# Revit family: Ventüer_VentilationLouvres_VL-50PL
name_source: partatom
category: Generic Models
units: mm (PartAtom-declared; Revit-internal decimal feet)

## family parameters
Always vertical = No
Can host rebar = No
Cut with Voids When Loaded = No
Part Type = Normal
Room Calculation Point = No
Round Connector Dimension = Use Diameter
Shared = No
Work Plane-Based = Yes

## types (2) — shared parameters
Aerodynamic Performance = VL-50PL1 – Coefficient of Entry: 0.281. VL-50PL2 – Coefficient of Entry: 0.285. VL-50PL3 – Coefficient of Entry: 0.253. VL-50PL4 – Coefficient of Entry: 0.287. VL-50PL5 – Coefficient of Entry: 0.258. VL-50PL6 – Coefficient of Entry: 0.264
Ancillaries = Bird Mesh, Insect Mesh, Solid Blanking, Perimeter Mounting Angle
Blade And Frame Gap = 16 mm
Blade Centres = 50 mm  [stored 0.164042 ft]
Blade Material = Ventüer Aluminium
Default Elevation = 1219 mm
Description = The Invisible Louvre
Exact Neck Height = 594 mm  [stored 1.94882 ft]
Exact Neck Height Check = 594 mm  [stored 1.94882 ft]
Exact Neck Width = 594 mm  [stored 1.94882 ft]
Exact Neck Width Check = 594 mm  [stored 1.94882 ft]
Face Panel = Ventüer Transparent
Frame Material = Ventüer Aluminium
Frame Set Count = 1
Frame Set Count Check = 2
Frame Set Transition Count = 1
Frame Set Transition Count Check = 2
Keynote = VL-50PL_FF
Manufacturer = Ventüer
Max Flow = 5000.0 L/s
Min Flow = 100.0 L/s
Model = VL-50PL
Multiple Frame Set = No
Multiple Transition = No
Noise Level NC Max = 0.00 NC
Noise Level NC Min = 0.00 NC
Nominal Height = 600 mm
Nominal Width = 600 mm
Nominated Air Flow = 100.0 L/s
Nominated Pessure Drop = 21.0 Pa
Rain Defence Performance = Class B – up to 1.0m/s suction velocity. Class C – up to 2.5m/s suction velocity. Class D – up to 3.5m/s suction velocity
Single Frame Set = Yes
Single Transition = No
Specified Air Flow = 0.0 L/s
Specified Pressure Drop = 21.0 Pa
Static Pressure Max = 60.0 Pa
Static Pressure Min = 10.0 Pa
URL = https://www.ventuer.co
Ventüer Product Range = Ventilation Louvres

## per-type parameters (varying)
| type | Base Width | Blade Count | Blade Cut Offset | Blade Length | Connector Height | Connector Width | Depth | Flanged | Frame Set Height | Frame Set Width | Glazed | Overall Opening Height | Overall Opening Width | Perforated Pattern Height | Perforated Pattern Width | Profile Width | Rear Frame Set Offset | Rear Mullion Offset | Single Frame Set Width | Top Blade Height |
| VL-50PL_FF | 52 mm | 9 | 450 mm  [stored 1.47638 ft] | 484 mm  [stored 1.58793 ft] | 490 mm  [stored 1.60761 ft] | 490 mm  [stored 1.60761 ft] | 101 mm  [stored 0.331365 ft] | Yes | 490 mm  [stored 1.60761 ft] | 490 mm  [stored 1.60761 ft] | No | 490 mm  [stored 1.60761 ft] | 490 mm  [stored 1.60761 ft] | 493 mm  [stored 1.61745 ft] | 493 mm  [stored 1.61745 ft] | 52 mm | 3 mm  [stored 0.00984252 ft] | 2 mm  [stored 0.00656168 ft] | 245 mm | 24 mm |
| VL-50PL_GF | 26 mm | 10 | 500 mm  [stored 1.64042 ft] | 536 mm | 542 mm  [stored 1.77822 ft] | 542 mm  [stored 1.77822 ft] | 105 mm  [stored 0.344488 ft] | No | 542 mm  [stored 1.77822 ft] | 542 mm  [stored 1.77822 ft] | Yes | 542 mm  [stored 1.77822 ft] | 542 mm  [stored 1.77822 ft] | 545 mm | 545 mm | 26 mm | 6 mm  [stored 0.019685 ft] | 0 mm  [stored 0 ft] | 271 mm | 26 mm |

note: [stored X ft] marks values corroborated as IEEE doubles in the binary element streams (Revit-internal decimal feet)

## geometry (parser evidence)
native form markers: Sweep x24
no freeform markers — native parametric forms only
